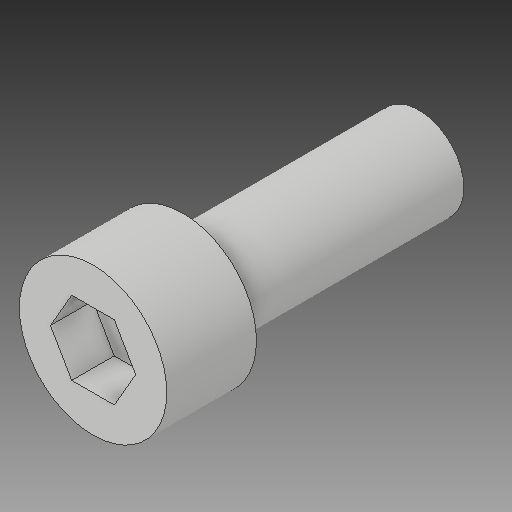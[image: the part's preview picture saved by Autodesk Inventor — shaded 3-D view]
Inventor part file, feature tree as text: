
AUTODESK INVENTOR PART (.ipt)
format: ipt  version: 2019 (Build 230136000, 136)  size: 128,512 bytes
history: native  units: in
note: dims shown in document units (in); Inventor stores cm internally (conversion verified against a paired STEP export)
features: other x12, extrude x3, sketch x3
ambient origin geometry x8: Origin, YZ Plane, XZ Plane, XY Plane, X Axis, Y Axis, Z Axis, Center Point
bodies: Solid1 (feature_tree)
feature tree (18):
  other  "Table"
  other  "shcs-10-0500"
  other  "shcs-10-0750"
  other  "shcs-10-1000"
  other  "shcs-10-1250"
  other  "shcs-10-1500"
  other  "shcs-10-1750"
  other  "shcs-10-2000"
  other  "shcs-10-2250"
  other  "shcs-10-2500"
  other  "shcs-10-2750"
  other  "shcs-10-3000"
  extrude  "Extrusion1"  TaperAngle=0.0deg  [1 undecoded]
  extrude  "Extrusion2"  [1 undecoded]
  extrude  "Extrusion3"  [1 undecoded]
  sketch  "Sketch1"  dims[d1=0.0in d4=0.0in]
  sketch  "Sketch2"  dims[d7=0.0in]
  sketch  "Sketch3"
note: 3 required parameter values undecoded (feature->parameter linkage not recoverable at this tier; creation-order binding heuristic only, values carry confidence <= 0.55)
